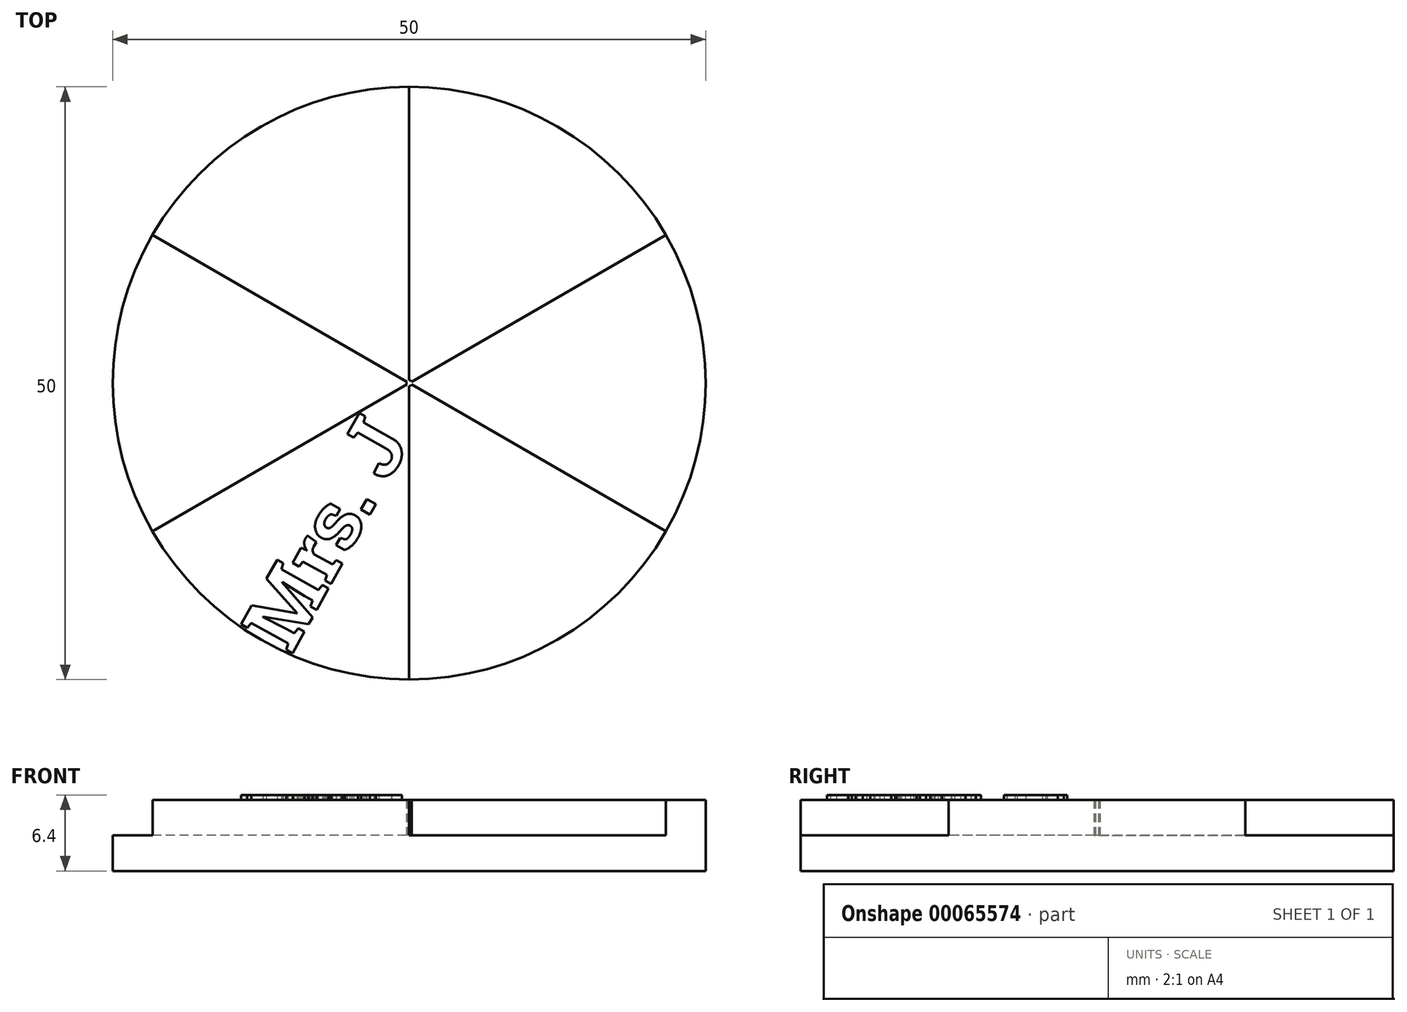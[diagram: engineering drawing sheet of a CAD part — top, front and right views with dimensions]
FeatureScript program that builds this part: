
annotation { "Feature Type Name" : "Feature", "Feature Type Description" : "" }
export const myFeature = defineFeature(function(context is Context, id is Id, definition is map)
    precondition{}
    {
        {
            var Q0;
            Q0=qCreatedBy(makeId("Top.planeOp"),FACE);
            var sketch = newSketch(context, id + "F0", { "sketchPlane" : qUnion([Q0])});
            skCircle(sketch, "E0", {"center": v(0, 0) * mm, "radius": 25 * mm});
            skSolve(sketch);
        }
        {
            var Q0;
            Q0 = qSketchRegion(id + "F0", true);
            extrude(context, id + "F1", {"entities" : qUnion([Q0]), "depth" : 3 * mm});
        }
        {
            var Q0;
            Q0=makeQuery(id+"F1.opExtrude","CAP_FACE",FACE,{"disambiguationData":[OSD([sQuery(id+"F0.wireOp",EDGE,"E0")])],"isStart":false});
            var sketch = newSketch(context, id + "F2", { "sketchPlane" : qUnion([Q0])});
            skLineSegment(sketch, "E1", {"start": v(0, 0.25) * mm, "end": v(0, 25) * mm});
            skLineSegment(sketch, "E2", {"start": v(0.21, 0.12) * mm, "end": v(21.65, 12.5) * mm});
            skLineSegment(sketch, "E3", {"start": v(0.21, -0.12) * mm, "end": v(21.65, -12.5) * mm});
            skLineSegment(sketch, "E4", {"start": v(-0.21, 0.12) * mm, "end": v(-21.65, 12.5) * mm});
            skLineSegment(sketch, "E5", {"start": v(0, -0.25) * mm, "end": v(0, -25) * mm});
            skLineSegment(sketch, "E6", {"start": v(-0.21, -0.12) * mm, "end": v(-21.65, -12.5) * mm});
            skCircle(sketch, "E7", {"center": v(0, 0) * mm, "radius": 0.25 * mm});
            skSolve(sketch);
        }
        {
            var Q0;
            {var subQ0=sQuery(id+"F2.wireOp",EDGE,"E1");Q0=makeQuery(id+"F2.imprint","IMPRINT",FACE,{"disambiguationData":[TD([[makeQuery(id+"F2.imprint","IMPRINT",EDGE,{"derivedFrom":subQ0}),1.0]])]});}
            var Q1;
            {var subQ0=sQuery(id+"F2.wireOp",EDGE,"E2");Q1=makeQuery(id+"F2.imprint","IMPRINT",FACE,{"disambiguationData":[TD([[makeQuery(id+"F2.imprint","IMPRINT",EDGE,{"derivedFrom":subQ0}),-1.0]])]});}
            var Q2;
            {var subQ0=sQuery(id+"F2.wireOp",EDGE,"E5");Q2=makeQuery(id+"F2.imprint","IMPRINT",FACE,{"disambiguationData":[TD([[makeQuery(id+"F2.imprint","IMPRINT",EDGE,{"derivedFrom":subQ0}),-1.0]])]});}
            var Q3;
            {var subQ0=sQuery(id+"F2.wireOp",EDGE,"E7");var subQ4=makeQuery(id+"F2.imprint","INTERSECT",VERTEX,{"derivedFrom":[sQuery(id+"F2.wireOp",EDGE,"E1"),subQ0]});Q3=makeQuery(id+"F2.imprint","IMPRINT",FACE,{"disambiguationData":[TD([[makeQuery(id+"F2.imprint","IMPRINT",EDGE,{"disambiguationData":[TD([[subQ4,1.0]])],"derivedFrom":subQ0}),1.0]])]});}
            extrude(context, id + "F3", {"entities" : qUnion([Q0, Q1, Q2, Q3]), "operationType" : NewBodyOperationType.ADD, "depth" : 3 * mm});
        }
        {
            var Q0;
            Q0=makeQuery(id+"F3.opExtrude","CAP_FACE",FACE,{"disambiguationData":[OSD([sQuery(id+"F0.wireOp",EDGE,"E0"),sQuery(id+"F2.wireOp",EDGE,"E1"),sQuery(id+"F2.wireOp",EDGE,"E2"),sQuery(id+"F2.wireOp",EDGE,"E3"),sQuery(id+"F2.wireOp",EDGE,"E4"),sQuery(id+"F2.wireOp",EDGE,"E5"),sQuery(id+"F2.wireOp",EDGE,"E6"),sQuery(id+"F2.wireOp",EDGE,"E7")])],"isStart":false});
            var sketch = newSketch(context, id + "F4", { "sketchPlane" : qUnion([Q0])});
            skText(sketch, "E8", { "text": "Mrs. J", "fontName": "RobotoSlab-Bold.ttf"});
            const initialGuessF4  = {"E8": [-0.00993, -0.02294, 0.48793, 0.87288, 0.00504]};
            skSetInitialGuess(sketch, initialGuessF4);
            skSolve(sketch);
        }
        {
            var Q0;
            Q0 = qSketchRegion(id + "F4", true);
            extrude(context, id + "F5", {"entities" : qUnion([Q0]), "operationType" : NewBodyOperationType.ADD, "depth" : 0.4 * mm});
        }
    });
